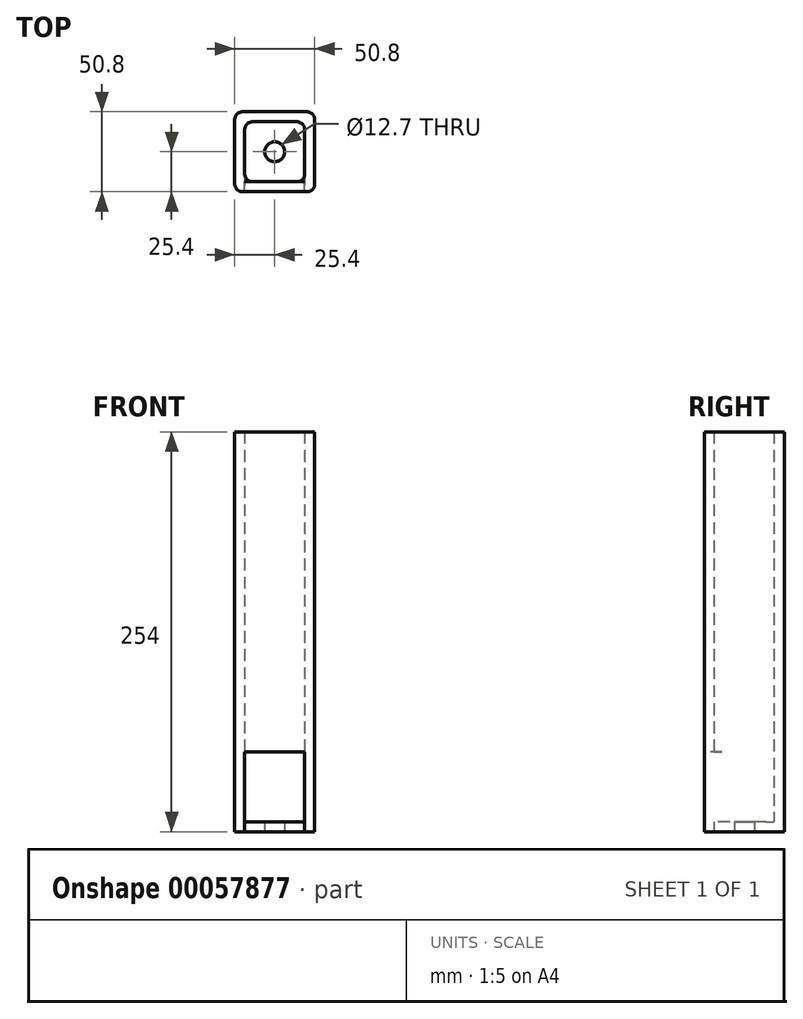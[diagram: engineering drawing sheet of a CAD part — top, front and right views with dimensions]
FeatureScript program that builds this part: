
annotation { "Feature Type Name" : "Feature", "Feature Type Description" : "" }
export const myFeature = defineFeature(function(context is Context, id is Id, definition is map)
    precondition{}
    {
        {
            var Q0;
            Q0=qCreatedBy(makeId("Top.planeOp"),FACE);
            var sketch = newSketch(context, id + "F0", { "sketchPlane" : qUnion([Q0])});
            skLineSegment(sketch, "E0.rect.bottom", {"start": v(25.4, -25.4) * mm, "end": v(-25.4, -25.4) * mm});
            skLineSegment(sketch, "E0.rect.top", {"start": v(25.4, 25.4) * mm, "end": v(-25.4, 25.4) * mm});
            skLineSegment(sketch, "E0.rect.left", {"start": v(25.4, -25.4) * mm, "end": v(25.4, 25.4) * mm});
            skLineSegment(sketch, "E0.rect.right", {"start": v(-25.4, -25.4) * mm, "end": v(-25.4, 25.4) * mm});
            skPoint(sketch, "E0.rect.middle", {"position": v(0, 0) * mm});
            skLineSegment(sketch, "E1.rect.bottom", {"start": v(19.05, -19.05) * mm, "end": v(-19.05, -19.05) * mm});
            skLineSegment(sketch, "E1.rect.top", {"start": v(19.05, 19.05) * mm, "end": v(-19.05, 19.05) * mm});
            skLineSegment(sketch, "E1.rect.left", {"start": v(19.05, -19.05) * mm, "end": v(19.05, 19.05) * mm});
            skLineSegment(sketch, "E1.rect.right", {"start": v(-19.05, -19.05) * mm, "end": v(-19.05, 19.05) * mm});
            skSolve(sketch);
        }
        {
            var Q0;
            Q0 = qSketchRegion(id + "F0", true);
            extrude(context, id + "F1", {"entities" : qUnion([Q0]), "depth" : 254 * mm});
        }
        {
            var Q0;
            Q0=makeQuery(id+"F1.opExtrude","SWEPT_FACE",FACE,{"disambiguationData":[OSD([sQuery(id+"F0.wireOp",EDGE,"E0.rect.bottom")])]});
            var sketch = newSketch(context, id + "F2", { "sketchPlane" : qUnion([Q0])});
            skLineSegment(sketch, "E2.bottom", {"start": v(-19.05, 0) * mm, "end": v(19.05, 0) * mm});
            skLineSegment(sketch, "E2.top", {"start": v(-19.05, 50.8) * mm, "end": v(19.05, 50.8) * mm});
            skLineSegment(sketch, "E2.left", {"start": v(-19.05, 0) * mm, "end": v(-19.05, 50.8) * mm});
            skLineSegment(sketch, "E2.right", {"start": v(19.05, 0) * mm, "end": v(19.05, 50.8) * mm});
            skSolve(sketch);
        }
        {
            var Q0;
            Q0 = qSketchRegion(id + "F2", true);
            extrude(context, id + "F3", {"entities" : qUnion([Q0]), "operationType" : NewBodyOperationType.REMOVE, "oppositeDirection" : true, "depth" : 6.35 * mm});
        }
        {
            var Q0;
            Q0=qCreatedBy(makeId("Top.planeOp"),FACE);
            var sketch = newSketch(context, id + "F4", { "sketchPlane" : qUnion([Q0])});
            skLineSegment(sketch, "E3.rect.bottom", {"start": v(19.05, 19.05) * mm, "end": v(-19.05, 19.05) * mm});
            skLineSegment(sketch, "E3.rect.top", {"start": v(19.05, -19.05) * mm, "end": v(-19.05, -19.05) * mm});
            skLineSegment(sketch, "E3.rect.left", {"start": v(19.05, 19.05) * mm, "end": v(19.05, -19.05) * mm});
            skLineSegment(sketch, "E3.rect.right", {"start": v(-19.05, 19.05) * mm, "end": v(-19.05, -19.05) * mm});
            skPoint(sketch, "E3.rect.middle", {"position": v(0, 0) * mm});
            skCircle(sketch, "E4", {"center": v(0, 0) * mm, "radius": 6.35 * mm});
            skSolve(sketch);
        }
        {
            var Q0;
            Q0 = qSketchRegion(id + "F4", true);
            extrude(context, id + "F5", {"entities" : qUnion([Q0]), "operationType" : NewBodyOperationType.ADD, "depth" : 6.35 * mm});
        }
        {
            var Q0;
            Q0=makeQuery(id+"F1.opExtrude","SWEPT_EDGE",EDGE,{"disambiguationData":[OSD([sQuery(id+"F0.wireOp",EDGE,"E0.rect.bottom"),sQuery(id+"F0.wireOp",EDGE,"E0.rect.right")])]});
            var Q1;
            Q1=makeQuery(id+"F1.opExtrude","SWEPT_EDGE",EDGE,{"disambiguationData":[OSD([sQuery(id+"F0.wireOp",EDGE,"E0.rect.top"),sQuery(id+"F0.wireOp",EDGE,"E0.rect.right")])]});
            var Q2;
            Q2=makeQuery(id+"F1.opExtrude","SWEPT_EDGE",EDGE,{"disambiguationData":[OSD([sQuery(id+"F0.wireOp",EDGE,"E0.rect.bottom"),sQuery(id+"F0.wireOp",EDGE,"E0.rect.left")])]});
            var Q3;
            Q3=makeQuery(id+"F1.opExtrude","SWEPT_EDGE",EDGE,{"disambiguationData":[OSD([sQuery(id+"F0.wireOp",EDGE,"E0.rect.top"),sQuery(id+"F0.wireOp",EDGE,"E0.rect.left")])]});
            var Q4;
            Q4=makeQuery(id+"F1.opExtrude","SWEPT_EDGE",EDGE,{"disambiguationData":[OSD([sQuery(id+"F0.wireOp",EDGE,"E1.rect.top"),sQuery(id+"F0.wireOp",EDGE,"E1.rect.right")])]});
            var Q5;
            Q5=makeQuery(id+"F1.opExtrude","SWEPT_EDGE",EDGE,{"disambiguationData":[OSD([sQuery(id+"F0.wireOp",EDGE,"E1.rect.top"),sQuery(id+"F0.wireOp",EDGE,"E1.rect.left")])]});
            var Q6;
            Q6=makeQuery(id+"F1.opExtrude","SWEPT_EDGE",EDGE,{"disambiguationData":[OSD([sQuery(id+"F0.wireOp",EDGE,"E1.rect.bottom"),sQuery(id+"F0.wireOp",EDGE,"E1.rect.right")])]});
            var Q7;
            Q7=makeQuery(id+"F1.opExtrude","SWEPT_EDGE",EDGE,{"disambiguationData":[OSD([sQuery(id+"F0.wireOp",EDGE,"E1.rect.bottom"),sQuery(id+"F0.wireOp",EDGE,"E1.rect.left")])]});
            fillet(context, id + "F6", {"entities" : qUnion([Q0, Q1, Q2, Q3, Q4, Q5, Q6, Q7]), "radius" : 5.08 * mm, "tangentPropagation" : true, "allowEdgeOverflow" : false});
        }
    });
